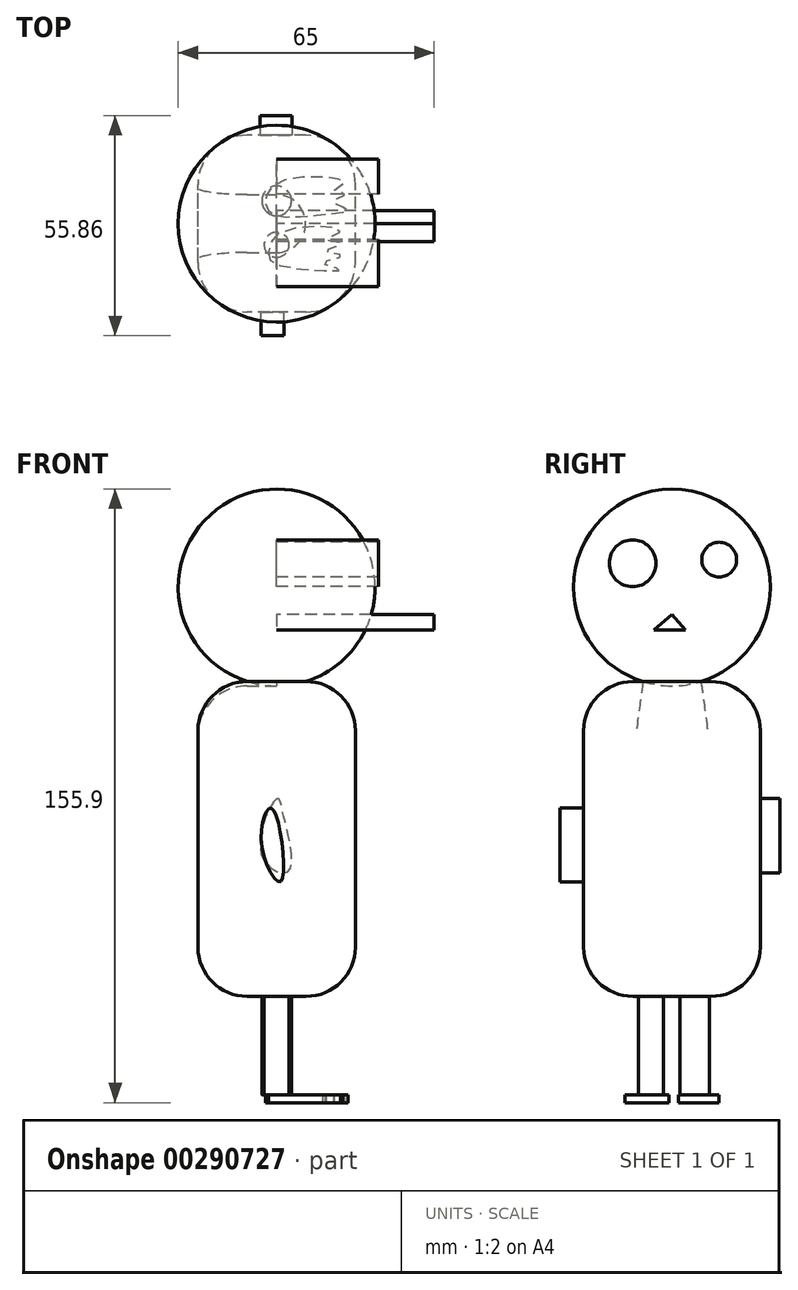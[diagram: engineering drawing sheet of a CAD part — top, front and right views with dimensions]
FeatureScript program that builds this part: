
annotation { "Feature Type Name" : "Feature", "Feature Type Description" : "" }
export const myFeature = defineFeature(function(context is Context, id is Id, definition is map)
    precondition{}
    {
        {
            var Q0;
            Q0=qCreatedBy(makeId("Front.planeOp"),FACE);
            var sketch = newSketch(context, id + "F0", { "sketchPlane" : qUnion([Q0])});
            skCircle(sketch, "E0", {"center": v(0, 37.34) * mm, "radius": 25 * mm});
            skSolve(sketch);
        }
        {
            var Q0;
            Q0=makeQuery(id+"F0.imprint","IMPRINT",FACE,{"disambiguationData":[TD([[makeQuery(id+"F0.imprint","IMPRINT",EDGE,{"derivedFrom":sQuery(id+"F0.wireOp",EDGE,"E0")}),1.0]])]});
            extrude(context, id + "F1", {"entities" : qUnion([Q0]), "depth" : 25 * mm});
        }
        {
            var Q0;
            Q0=makeQuery(id+"F1.opExtrude","CAP_FACE",FACE,{"disambiguationData":[OSD([sQuery(id+"F0.wireOp",EDGE,"E0")])],"isStart":true});
            extrude(context, id + "F2", {"entities" : qUnion([Q0]), "operationType" : NewBodyOperationType.ADD, "depth" : 25 * mm});
        }
        {
            var Q0;
            Q0=makeQuery(id+"F2.opExtrude","CAP_EDGE",EDGE,{"disambiguationData":[OSD([sQuery(id+"F0.wireOp",EDGE,"E0")])],"isStart":false});
            var Q1;
            Q1=makeQuery(id+"F1.opExtrude","CAP_EDGE",EDGE,{"disambiguationData":[OSD([sQuery(id+"F0.wireOp",EDGE,"E0")])],"isStart":false});
            var Q2;
            {var subQ0=sQuery(id+"F0.wireOp",EDGE,"E0");Q2=makeQuery(id+"F2.boolean.opBoolean","MERGE",FACE,{"derivedFrom":[makeQuery(id+"F1.opExtrude","SWEPT_FACE",FACE,{"disambiguationData":[OSD([subQ0])]}),makeQuery(id+"F2.opExtrude","SWEPT_FACE",FACE,{"disambiguationData":[OSD([subQ0])]})]});}
            fillet(context, id + "F3", {"entities" : qUnion([Q0, Q1, Q2]), "radius" : 25 * mm, "tangentPropagation" : true, "allowEdgeOverflow" : false});
        }
        {
            var Q0;
            Q0=qCreatedBy(makeId("Right.planeOp"),FACE);
            var sketch = newSketch(context, id + "F4", { "sketchPlane" : qUnion([Q0])});
            skLineSegment(sketch, "E1", {"start": v(0, 30.47) * mm, "end": v(-4.57, 26.54) * mm});
            skLineSegment(sketch, "E2", {"start": v(0, 30.47) * mm, "end": v(1.69, 28.5) * mm});
            skPoint(sketch, "E2.endSnap0", {"position": v(-2.28, 28.5) * mm});
            skLineSegment(sketch, "E3", {"start": v(1.69, 28.5) * mm, "end": v(3.38, 26.54) * mm});
            skLineSegment(sketch, "E4", {"start": v(3.38, 26.54) * mm, "end": v(-4.57, 26.54) * mm});
            skSolve(sketch);
        }
        {
            var Q0;
            Q0 = qSketchRegion(id + "F4", true);
            extrude(context, id + "F5", {"entities" : qUnion([Q0]), "depth" : 40 * mm});
        }
        {
            var Q0;
            Q0=qCreatedBy(makeId("Right.planeOp"),FACE);
            var sketch = newSketch(context, id + "F6", { "sketchPlane" : qUnion([Q0])});
            skCircle(sketch, "E5", {"center": v(-10, 43.49) * mm, "radius": 5.94 * mm});
            skCircle(sketch, "E6", {"center": v(11.98, 44.41) * mm, "radius": 4.43 * mm});
            skSolve(sketch);
        }
        {
            var Q0;
            Q0 = qSketchRegion(id + "F6", true);
            extrude(context, id + "F7", {"entities" : qUnion([Q0]), "depth" : 25.9 * mm});
        }
        {
            var Q0;
            Q0=qCreatedBy(makeId("Right.planeOp"),FACE);
            var sketch = newSketch(context, id + "F8", { "sketchPlane" : qUnion([Q0])});
            skLineSegment(sketch, "E7.bottom", {"start": v(-22.43, 13.44) * mm, "end": v(22.43, 13.44) * mm});
            skLineSegment(sketch, "E7.top", {"start": v(-22.43, -66.56) * mm, "end": v(22.43, -66.56) * mm});
            skLineSegment(sketch, "E7.left", {"start": v(-22.43, 13.44) * mm, "end": v(-22.43, -66.56) * mm});
            skLineSegment(sketch, "E7.right", {"start": v(22.43, 13.44) * mm, "end": v(22.43, -66.56) * mm});
            skPoint(sketch, "E7.middle", {"position": v(0, -26.56) * mm});
            skSolve(sketch);
        }
        {
            var Q0;
            Q0=makeQuery(id+"F8.imprint","IMPRINT",FACE,{"disambiguationData":[TD([[makeQuery(id+"F8.imprint","IMPRINT",EDGE,{"derivedFrom":sQuery(id+"F8.wireOp",EDGE,"E7.bottom")}),-1.0]])]});
            extrude(context, id + "F9", {"entities" : qUnion([Q0]), "operationType" : NewBodyOperationType.ADD, "depth" : 20 * mm});
        }
        {
            var Q0;
            Q0=makeQuery(id+"F9.opExtrude","CAP_FACE",FACE,{"disambiguationData":[OSD([sQuery(id+"F8.wireOp",EDGE,"E7.bottom"),sQuery(id+"F8.wireOp",EDGE,"E7.top"),sQuery(id+"F8.wireOp",EDGE,"E7.left"),sQuery(id+"F8.wireOp",EDGE,"E7.right")])],"isStart":true});
            extrude(context, id + "F10", {"entities" : qUnion([Q0]), "operationType" : NewBodyOperationType.ADD, "depth" : 20 * mm});
        }
        {
            var Q0;
            Q0=makeQuery(id+"F9.opExtrude","CAP_EDGE",EDGE,{"disambiguationData":[OSD([sQuery(id+"F8.wireOp",EDGE,"E7.bottom")])],"isStart":false});
            var Q1;
            Q1=makeQuery(id+"F9.opExtrude","CAP_FACE",FACE,{"disambiguationData":[OSD([sQuery(id+"F8.wireOp",EDGE,"E7.bottom"),sQuery(id+"F8.wireOp",EDGE,"E7.top"),sQuery(id+"F8.wireOp",EDGE,"E7.left"),sQuery(id+"F8.wireOp",EDGE,"E7.right")])],"isStart":false});
            var Q2;
            {var subQ0=sQuery(id+"F8.wireOp",EDGE,"E7.right");var subQ1=sQuery(id+"F8.wireOp",EDGE,"E7.bottom");Q2=makeQuery(id+"F10.boolean.opBoolean","MERGE",EDGE,{"derivedFrom":[makeQuery(id+"F9.opExtrude","SWEPT_EDGE",EDGE,{"disambiguationData":[OSD([subQ1,subQ0])]}),makeQuery(id+"F10.opExtrude","SWEPT_EDGE",EDGE,{"disambiguationData":[OSD([subQ1,subQ0])]})]});}
            var Q3;
            {var subQ0=sQuery(id+"F8.wireOp",EDGE,"E7.right");Q3=makeQuery(id+"F10.boolean.opBoolean","MERGE",FACE,{"derivedFrom":[makeQuery(id+"F9.opExtrude","SWEPT_FACE",FACE,{"disambiguationData":[OSD([subQ0])]}),makeQuery(id+"F10.opExtrude","SWEPT_FACE",FACE,{"disambiguationData":[OSD([subQ0])]})]});}
            var Q4;
            {var subQ0=sQuery(id+"F8.wireOp",EDGE,"E7.left");Q4=makeQuery(id+"F10.boolean.opBoolean","MERGE",FACE,{"derivedFrom":[makeQuery(id+"F9.opExtrude","SWEPT_FACE",FACE,{"disambiguationData":[OSD([subQ0])]}),makeQuery(id+"F10.opExtrude","SWEPT_FACE",FACE,{"disambiguationData":[OSD([subQ0])]})]});}
            var Q5;
            Q5=makeQuery(id+"F10.opExtrude","CAP_FACE",FACE,{"disambiguationData":[OSD([sQuery(id+"F8.wireOp",EDGE,"E7.bottom"),sQuery(id+"F8.wireOp",EDGE,"E7.top"),sQuery(id+"F8.wireOp",EDGE,"E7.left"),sQuery(id+"F8.wireOp",EDGE,"E7.right")])],"isStart":false});
            fillet(context, id + "F11", {"entities" : qUnion([Q0, Q1, Q2, Q3, Q4, Q5]), "radius" : 12.5 * mm, "tangentPropagation" : true, "allowEdgeOverflow" : false});
        }
        {
            var Q0;
            {var subQ0=sQuery(id+"F8.wireOp",EDGE,"E7.left");Q0=makeQuery(id+"F10.boolean.opBoolean","MERGE",FACE,{"derivedFrom":[makeQuery(id+"F9.opExtrude","SWEPT_FACE",FACE,{"disambiguationData":[OSD([subQ0])]}),makeQuery(id+"F10.opExtrude","SWEPT_FACE",FACE,{"disambiguationData":[OSD([subQ0])]})]});}
            var sketch = newSketch(context, id + "F12", { "sketchPlane" : qUnion([Q0])});
            skFitSpline(sketch, "E8", {"points": [v(-1.94, -18.84) * mm, v(-3.7, -29.03) * mm, v(1.07, -37.34) * mm, v(0, -21.03) * mm, v(-1.94, -18.84) * mm]});
            skSolve(sketch);
        }
        {
            var Q0;
            Q0 = qSketchRegion(id + "F12", true);
            extrude(context, id + "F13", {"entities" : qUnion([Q0]), "depth" : 6 * mm});
        }
        {
            var Q0;
            {var subQ0=sQuery(id+"F8.wireOp",EDGE,"E7.right");Q0=makeQuery(id+"F10.boolean.opBoolean","MERGE",FACE,{"derivedFrom":[makeQuery(id+"F9.opExtrude","SWEPT_FACE",FACE,{"disambiguationData":[OSD([subQ0])]}),makeQuery(id+"F10.opExtrude","SWEPT_FACE",FACE,{"disambiguationData":[OSD([subQ0])]})]});}
            var sketch = newSketch(context, id + "F14", { "sketchPlane" : qUnion([Q0])});
            skFitSpline(sketch, "E9", {"points": [v(0, -16.37) * mm, v(3.9, -30.4) * mm, v(-2.96, -34.77) * mm, v(-1.61, -19.9) * mm, v(0, -16.37) * mm]});
            skSolve(sketch);
        }
        {
            var Q0;
            Q0 = qSketchRegion(id + "F14", true);
            extrude(context, id + "F15", {"entities" : qUnion([Q0]), "depth" : 5 * mm});
        }
        {
            var Q0;
            {var subQ0=sQuery(id+"F8.wireOp",EDGE,"E7.top");Q0=makeQuery(id+"F10.boolean.opBoolean","MERGE",FACE,{"derivedFrom":[makeQuery(id+"F9.opExtrude","SWEPT_FACE",FACE,{"disambiguationData":[OSD([subQ0])]}),makeQuery(id+"F10.opExtrude","SWEPT_FACE",FACE,{"disambiguationData":[OSD([subQ0])]})]});}
            var sketch = newSketch(context, id + "F16", { "sketchPlane" : qUnion([Q0])});
            skCircle(sketch, "E10", {"center": v(0, 5.37) * mm, "radius": 3.18 * mm});
            skCircle(sketch, "E11", {"center": v(0, -5.8) * mm, "radius": 3.77 * mm});
            skPoint(sketch, "E11.centerSnap0", {"position": v(0, 9.93) * mm});
            skSolve(sketch);
        }
        {
            var Q0;
            Q0 = qSketchRegion(id + "F16", true);
            extrude(context, id + "F17", {"entities" : qUnion([Q0]), "operationType" : NewBodyOperationType.ADD, "depth" : 25 * mm});
        }
        {
            var Q0;
            Q0=makeQuery(id+"F17.opExtrude","CAP_FACE",FACE,{"disambiguationData":[OSD([sQuery(id+"F16.wireOp",EDGE,"E10")])],"isStart":false});
            cPlane(context, id + "F18", {"entities" : qUnion([Q0]), "cplaneType" : CPlaneType.OFFSET, "offset" : 0 * mm, "width" : 150 * mm, "height" : 150 * mm});
        }
        {
            var Q0;
            Q0=qCreatedBy(id+"F18.planeOp",FACE);
            var sketch = newSketch(context, id + "F19", { "sketchPlane" : qUnion([Q0])});
            skFitSpline(sketch, "E12", {"points": [v(-2.06, 7.25) * mm, v(0, 10.37) * mm, v(16.13, 11.7) * mm, v(11.82, 10.04) * mm, v(16.75, 8.13) * mm, v(12.4, 7.01) * mm, v(16.77, 5.05) * mm, v(12.71, 4.15) * mm, v(16.24, 1.9) * mm, v(1.38, 2.04) * mm, v(-2.06, 7.25) * mm]});
            skFitSpline(sketch, "E13", {"points": [v(-2.8, -5.1) * mm, v(0, -2.09) * mm, v(14.6, -2.66) * mm, v(18, -3.53) * mm, v(14.6, -5.6) * mm, v(17.31, -7.5) * mm, v(14.72, -8.54) * mm, v(17.2, -10.34) * mm, v(1.44, -10.94) * mm, v(-2.8, -5.1) * mm]});
            skSolve(sketch);
        }
        {
            var Q0;
            Q0 = qSketchRegion(id + "F19", true);
            extrude(context, id + "F20", {"entities" : qUnion([Q0]), "depth" : 2 * mm});
        }
    });
